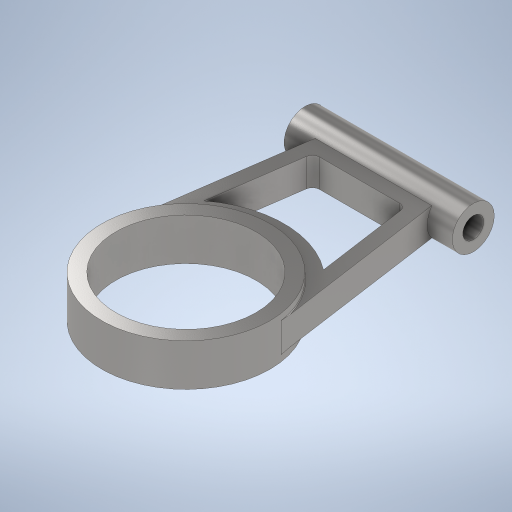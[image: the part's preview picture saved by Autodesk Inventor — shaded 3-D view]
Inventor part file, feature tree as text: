
AUTODESK INVENTOR PART (.ipt)
format: ipt  version: 2024 (Build 280153000, 153)  size: 331,776 bytes
history: native  units: mm
features: sketch x3, extrude x3, fillet x3, revolve x1, hole x1, projected_geometry x1
ambient origin geometry x8: Origin, YZ Plane, XZ Plane, XY Plane, X Axis, Y Axis, Z Axis, Center Point
bodies: Body1 (feature_tree)
feature tree (12):
  sketch  "Skizze1"  dims[d0=100.0mm d1=120.0mm]
  extrude  "Extrusion3"  Depth=120.0mm
  extrude  "Extrusion4"  Depth=120.0mm
  revolve  "Umdrehung2"
  hole  "Bohrung1"  [1 undecoded]
  extrude  "Extrusion5"  Depth=0.5mm TaperAngle=0.0deg
  fillet  "Rundung1"  Radius=30.0mm
  fillet  "Rundung2"  [1 undecoded]
  fillet  "Rundung3"  Radius=10.0mm
  sketch  "Skizze3"  dims[d2=30.0mm d3=120.0mm]
  sketch  "Skizze4"  dims[d4=80.0mm d5=160.0mm d11=20.0mm d12=0.0mm d13=30.0mm d14=0.0mm d15=90.0deg d17=15.0mm d18=6.0mm d19=4.0mm d20=2.0mm d21=90.0deg d22=8.0mm d23=20.594885mm d24=10.0mm d25=70.0mm d27=10.0mm d28=10.0mm d29=30.0mm d30=0.0mm d31=5.0mm d32=0.5mm d33=0.5mm]
  projected_geometry  "Projizierte Kontur1"
note: 2 required parameter values undecoded (feature->parameter linkage not recoverable at this tier; creation-order binding heuristic only, values carry confidence <= 0.55)
